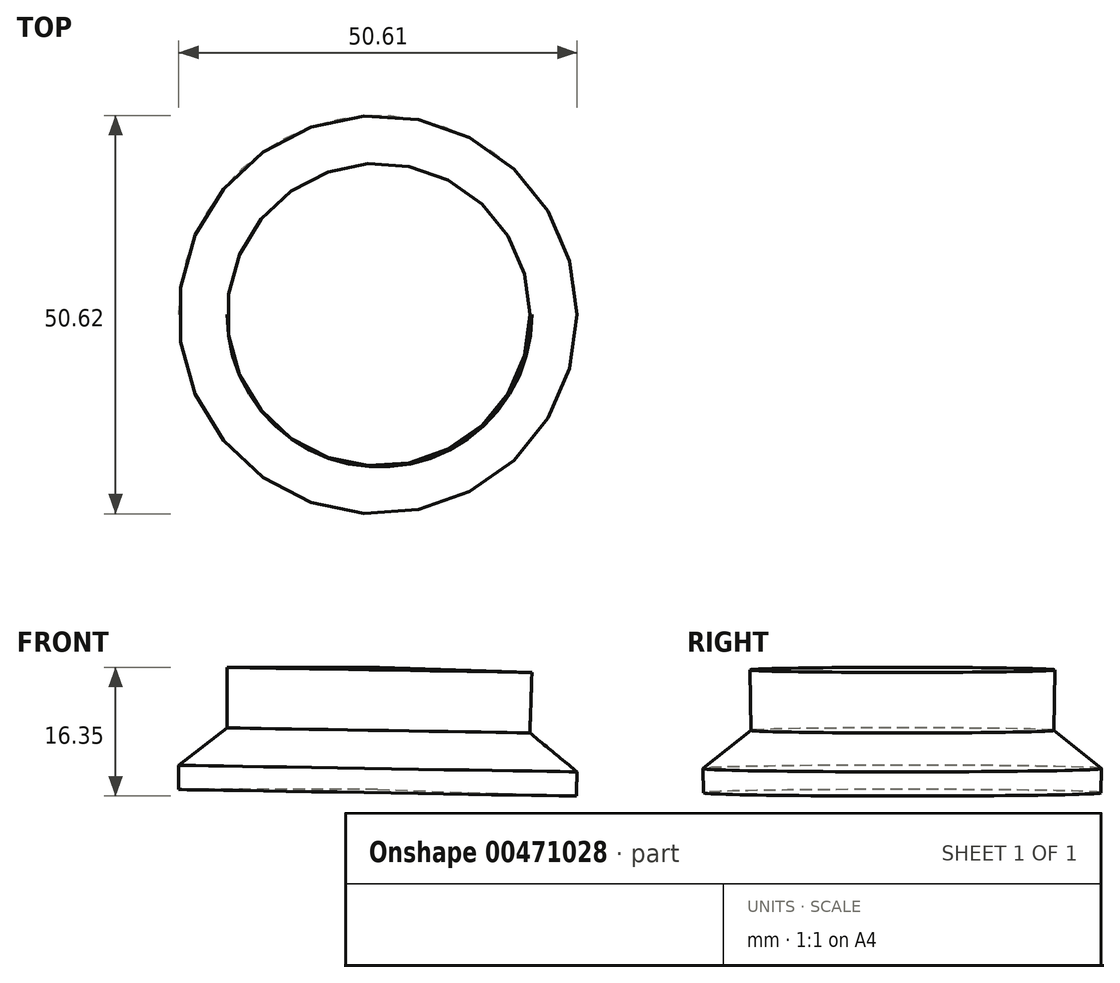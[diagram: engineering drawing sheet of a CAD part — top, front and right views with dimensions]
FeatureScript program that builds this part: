
annotation { "Feature Type Name" : "Feature", "Feature Type Description" : "" }
export const myFeature = defineFeature(function(context is Context, id is Id, definition is map)
    precondition{}
    {
        {
            var Q0;
            Q0=qCreatedBy(makeId("Front.planeOp"),FACE);
            var sketch = newSketch(context, id + "F0", { "sketchPlane" : qUnion([Q0])});
            skLineSegment(sketch, "E0", {"start": v(-10.3, 4.35) * mm, "end": v(-35.56, 4.35) * mm});
            skLineSegment(sketch, "E1", {"start": v(-35.56, 4.35) * mm, "end": v(-35.56, 7.42) * mm});
            skLineSegment(sketch, "E2", {"start": v(-35.56, 7.42) * mm, "end": v(-29.4, 12.17) * mm});
            skLineSegment(sketch, "E3", {"start": v(-29.4, 12.17) * mm, "end": v(-29.4, 19.86) * mm});
            skLineSegment(sketch, "E4", {"start": v(-29.4, 19.86) * mm, "end": v(-10.04, 19.86) * mm});
            skLineSegment(sketch, "E5", {"start": v(-10.04, 19.86) * mm, "end": v(-10.3, 4.35) * mm});
            skSolve(sketch);
        }
        {
            var Q0;
            Q0=makeQuery(id+"F0.imprint","IMPRINT",FACE,{"disambiguationData":[TD([[makeQuery(id+"F0.imprint","IMPRINT",EDGE,{"derivedFrom":sQuery(id+"F0.wireOp",EDGE,"E0")}),-1.0]])]});
            var Q1;
            Q1=sQuery(id+"F0.wireOp",EDGE,"E5");
            revolve(context, id + "F1", {"entities" : qUnion([Q0]), "axis" : qUnion([Q1]), "revolveType" : RevolveType.FULL});
        }
    });
